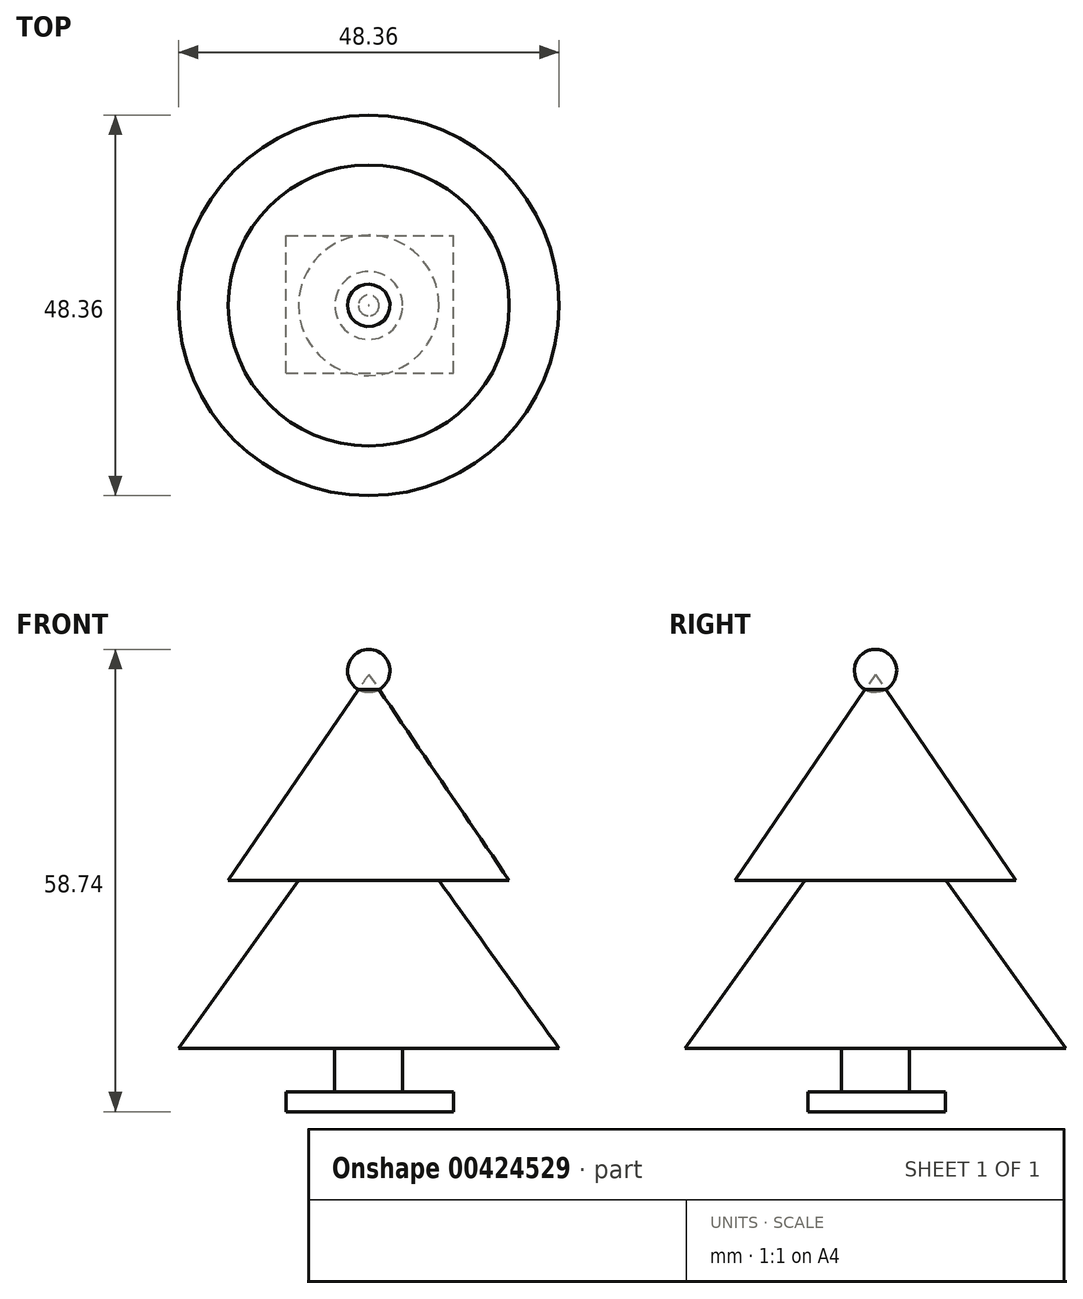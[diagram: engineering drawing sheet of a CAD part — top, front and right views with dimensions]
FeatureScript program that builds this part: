
annotation { "Feature Type Name" : "Feature", "Feature Type Description" : "" }
export const myFeature = defineFeature(function(context is Context, id is Id, definition is map)
    precondition{}
    {
        {
            var Q0;
            Q0=qCreatedBy(makeId("Front.planeOp"),FACE);
            var sketch = newSketch(context, id + "F0", { "sketchPlane" : qUnion([Q0])});
            skLineSegment(sketch, "E0", {"start": v(0, 55.55) * mm, "end": v(17.84, 29.36) * mm});
            skLineSegment(sketch, "E1", {"start": v(17.84, 29.36) * mm, "end": v(0, 29.36) * mm});
            skLineSegment(sketch, "E2", {"start": v(8.92, 29.36) * mm, "end": v(24.18, 8.06) * mm});
            skLineSegment(sketch, "E3", {"start": v(24.18, 8.06) * mm, "end": v(0, 8.06) * mm});
            skLineSegment(sketch, "E4", {"start": v(4.32, 8.06) * mm, "end": v(4.32, 0) * mm});
            skLineSegment(sketch, "E5", {"start": v(4.32, 0) * mm, "end": v(0, 0) * mm});
            skLineSegment(sketch, "E6", {"start": v(0, 75.7) * mm, "end": v(0, -75.4) * mm});
            skArc(sketch, "E7", {"start": v(0, 53.3) * mm, "mid": v(2.74, 56.02) * mm, "end": v(0, 58.74) * mm});
            skSolve(sketch);
        }
        {
            var Q0;
            {var subQ4=sQuery(id+"F0.wireOp",EDGE,"E2");Q0=makeQuery(id+"F0.imprint","IMPRINT",FACE,{"disambiguationData":[TD([[makeQuery(id+"F0.imprint","IMPRINT",EDGE,{"derivedFrom":subQ4}),-1.0]])]});}
            var Q1;
            {var subQ1=sQuery(id+"F0.wireOp",EDGE,"E5");Q1=makeQuery(id+"F0.imprint","IMPRINT",FACE,{"disambiguationData":[TD([[makeQuery(id+"F0.imprint","IMPRINT",EDGE,{"derivedFrom":subQ1}),1.0]])]});}
            var Q2;
            {var subQ3=sQuery(id+"F0.wireOp",EDGE,"E4");Q2=makeQuery(id+"F0.imprint","IMPRINT",FACE,{"disambiguationData":[TD([[makeQuery(id+"F0.imprint","IMPRINT",EDGE,{"derivedFrom":subQ3}),-1.0]])]});}
            var Q3;
            {var subQ0=sQuery(id+"F0.wireOp",EDGE,"xpxnCqK1-7LCT-S4Jh-9hrC-CvwYRl6KbJ1F");var subQ1=sQuery(id+"F0.wireOp",EDGE,"E6");var subQ3=makeQuery(id+"F0.imprint","INTERSECT",VERTEX,{"derivedFrom":[subQ1,subQ0]});Q3=makeQuery(id+"F0.imprint","IMPRINT",FACE,{"disambiguationData":[TD([[makeQuery(id+"F0.imprint","IMPRINT",EDGE,{"disambiguationData":[TD([[subQ3,-1.0]])],"derivedFrom":subQ1}),-1.0]])]});}
            var Q4;
            {var subQ0=sQuery(id+"F0.wireOp",EDGE,"E6");var subQ1=sQuery(id+"F0.wireOp",EDGE,"E0");var subQ2=makeQuery(id+"F0.imprint","INTERSECT",VERTEX,{"derivedFrom":[subQ1,subQ0]});Q4=makeQuery(id+"F0.imprint","IMPRINT",FACE,{"disambiguationData":[TD([[makeQuery(id+"F0.imprint","IMPRINT",EDGE,{"disambiguationData":[TD([[subQ2,-1.0]])],"derivedFrom":subQ1}),1.0]])]});}
            var Q5;
            {var subQ1=sQuery(id+"F0.wireOp",EDGE,"E1");var subQ4=sQuery(id+"F0.wireOp",EDGE,"E0");var subQ5=makeQuery(id+"F0.imprint","INTERSECT",VERTEX,{"derivedFrom":[subQ4,subQ1]});Q5=makeQuery(id+"F0.imprint","IMPRINT",FACE,{"disambiguationData":[TD([[makeQuery(id+"F0.imprint","IMPRINT",EDGE,{"disambiguationData":[TD([[subQ5,1.0]])],"derivedFrom":subQ4}),-1.0]])]});}
            var Q6;
            Q6=sQuery(id+"F0.wireOp",EDGE,"E6");
            revolve(context, id + "F1", {"entities" : qUnion([Q0, Q1, Q2, Q3, Q4, Q5]), "axis" : qUnion([Q6]), "revolveType" : RevolveType.FULL});
        }
        {
            var Q0;
            Q0=qCreatedBy(makeId("Top.planeOp"),FACE);
            var sketch = newSketch(context, id + "F2", { "sketchPlane" : qUnion([Q0])});
            skLineSegment(sketch, "E8.bottom", {"start": v(-10.5, -8.6) * mm, "end": v(10.78, -8.6) * mm});
            skLineSegment(sketch, "E8.top", {"start": v(-10.5, 8.9) * mm, "end": v(10.78, 8.9) * mm});
            skLineSegment(sketch, "E8.left", {"start": v(-10.5, -8.6) * mm, "end": v(-10.5, 8.9) * mm});
            skLineSegment(sketch, "E8.right", {"start": v(10.78, -8.6) * mm, "end": v(10.78, 8.9) * mm});
            skSolve(sketch);
        }
        {
            var Q0;
            Q0=makeQuery(id+"F2.imprint","IMPRINT",FACE,{"disambiguationData":[TD([[makeQuery(id+"F2.imprint","IMPRINT",EDGE,{"derivedFrom":sQuery(id+"F2.wireOp",EDGE,"eEArg8Id-dm6A-yWGQ-JYhr-3TSg2mfsqwa7.bottom")}),1.0]])]});
            var Q1;
            Q1=makeQuery(id+"F2.imprint","IMPRINT",FACE,{"disambiguationData":[TD([[makeQuery(id+"F2.imprint","IMPRINT",EDGE,{"derivedFrom":sQuery(id+"F2.wireOp",EDGE,"E8.bottom")}),1.0]])]});
            extrude(context, id + "F3", {"entities" : qUnion([Q0, Q1]), "operationType" : NewBodyOperationType.ADD, "depth" : 2.54 * mm});
        }
    });
